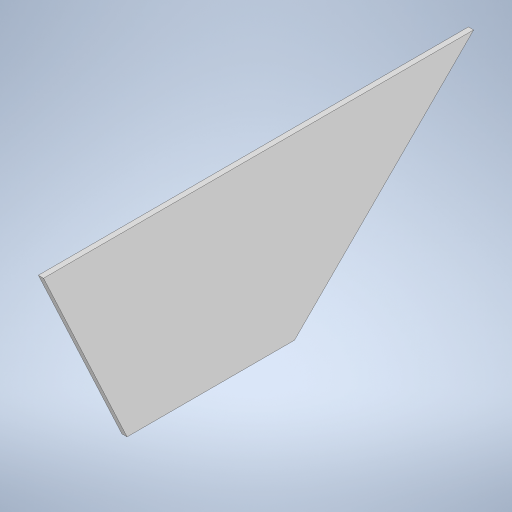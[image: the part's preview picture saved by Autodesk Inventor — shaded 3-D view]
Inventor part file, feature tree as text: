
AUTODESK INVENTOR PART (.ipt)
format: ipt  version: 2024.3 (Build 283343000, 343)  size: 211,456 bytes
history: native  units: mm
features: extrude x1, sketch x1
ambient origin geometry x8: Origin, YZ Plane, XZ Plane, XY Plane, X Axis, Y Axis, Z Axis, Center Point
bodies: Solid1 (feature_tree)
feature tree (2):
  extrude  "Extrusion1"  Depth=114.554mm
  sketch  "Sketch1"  dims[d0=97.0mm d1=114.554mm d2=45.0deg d3=4.363323mm d4=3.0mm d5=0.0mm]
